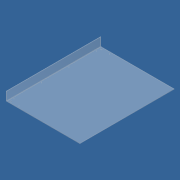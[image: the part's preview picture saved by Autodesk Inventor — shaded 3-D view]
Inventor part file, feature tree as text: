
AUTODESK INVENTOR PART (.ipt)
format: ipt  version: 2012 (Build 160160000, 160)  size: 103,424 bytes
history: native  units: in
note: dims shown in document units (in); Inventor stores cm internally (conversion verified against a paired STEP export)
features: hole x3, pattern_linear x3, extrude x1, sketch x1
ambient origin geometry x8: Origin, YZ Plane, XZ Plane, XY Plane, X Axis, Y Axis, Z Axis, Center Point
bodies: Solid1 (feature_tree)
feature tree (8):
  extrude  "Extrusion1"  Depth=0.25in
  hole  "Hole1"  [1 undecoded]
  pattern_linear  "Rectangular Pattern1"  Spacing1=37.5in  [1 undecoded]
  hole  "Hole2"  [1 undecoded]
  pattern_linear  "Rectangular Pattern2"  Spacing1=0.1875in  [1 undecoded]
  hole  "Hole3"  [1 undecoded]
  pattern_linear  "Rectangular Pattern3"  Count1=4 Spacing1=14.0in
  sketch  "Sketch1"  dims[d0=4.5in d1=0.25in d2=0.25in d3=37.5in d4=0.125in d5=0.1875in d6=48.0in d7=0.0in d8=3.0in d9=0.625in d10=0.265in d11=0.75in d12=0.375in d13=0.25in d14=0.5635in d15=1.0in d16=0.8108in d17=1.5748in d19=14.0in d20=1.0in d21=1.5in d22=0.5in d23=0.75in d24=0.375in d25=0.25in d26=0.5635in d27=1.0in d28=0.8108in d29=0.7874in d31=46.0in d32=1.0in d33=5.5in d34=0.1875in d35=0.75in d36=0.375in d37=0.25in d38=0.5635in d39=1.0in d40=0.8108in d41=0.7874in d43=46.0in]
note: 5 required parameter values undecoded (feature->parameter linkage not recoverable at this tier; creation-order binding heuristic only, values carry confidence <= 0.55)
